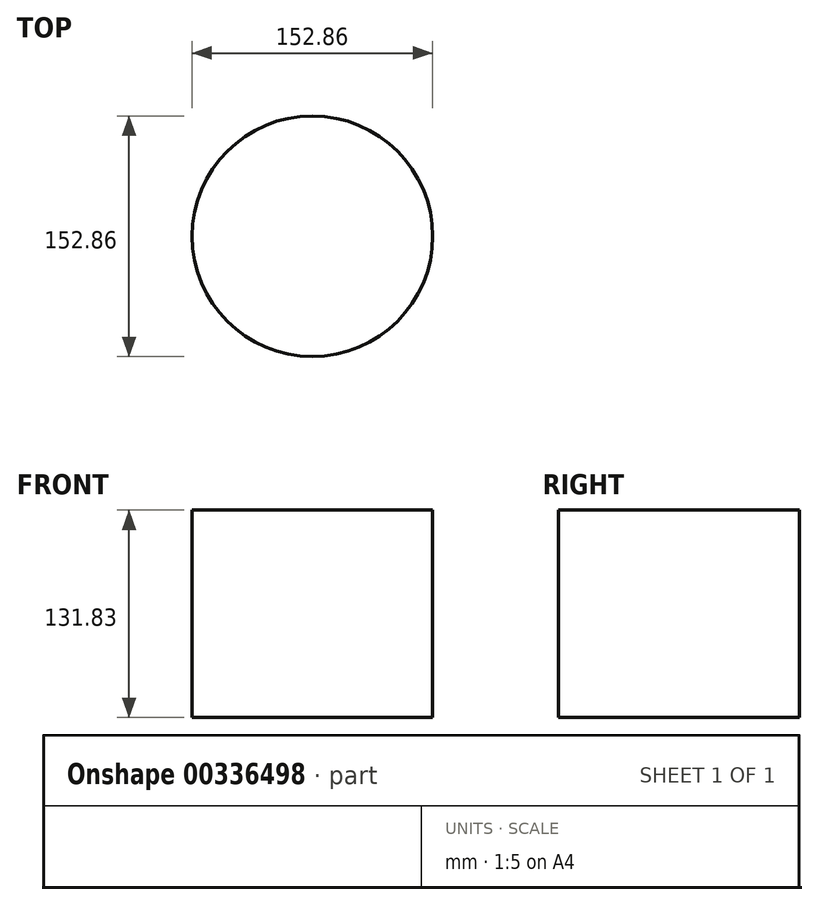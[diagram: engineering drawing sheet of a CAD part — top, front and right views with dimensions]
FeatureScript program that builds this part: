
annotation { "Feature Type Name" : "Feature", "Feature Type Description" : "" }
export const myFeature = defineFeature(function(context is Context, id is Id, definition is map)
    precondition{}
    {
        {
            var Q0;
            Q0=qCreatedBy(makeId("Top.planeOp"),FACE);
            var sketch = newSketch(context, id + "F0", { "sketchPlane" : qUnion([Q0])});
            skCircle(sketch, "E0", {"center": v(0, 0) * mm, "radius": 76.43 * mm});
            skSolve(sketch);
        }
        {
            var Q0;
            Q0 = qSketchRegion(id + "F0", true);
            extrude(context, id + "F1", {"entities" : qUnion([Q0]), "depth" : 131.83 * mm});
        }
    });
